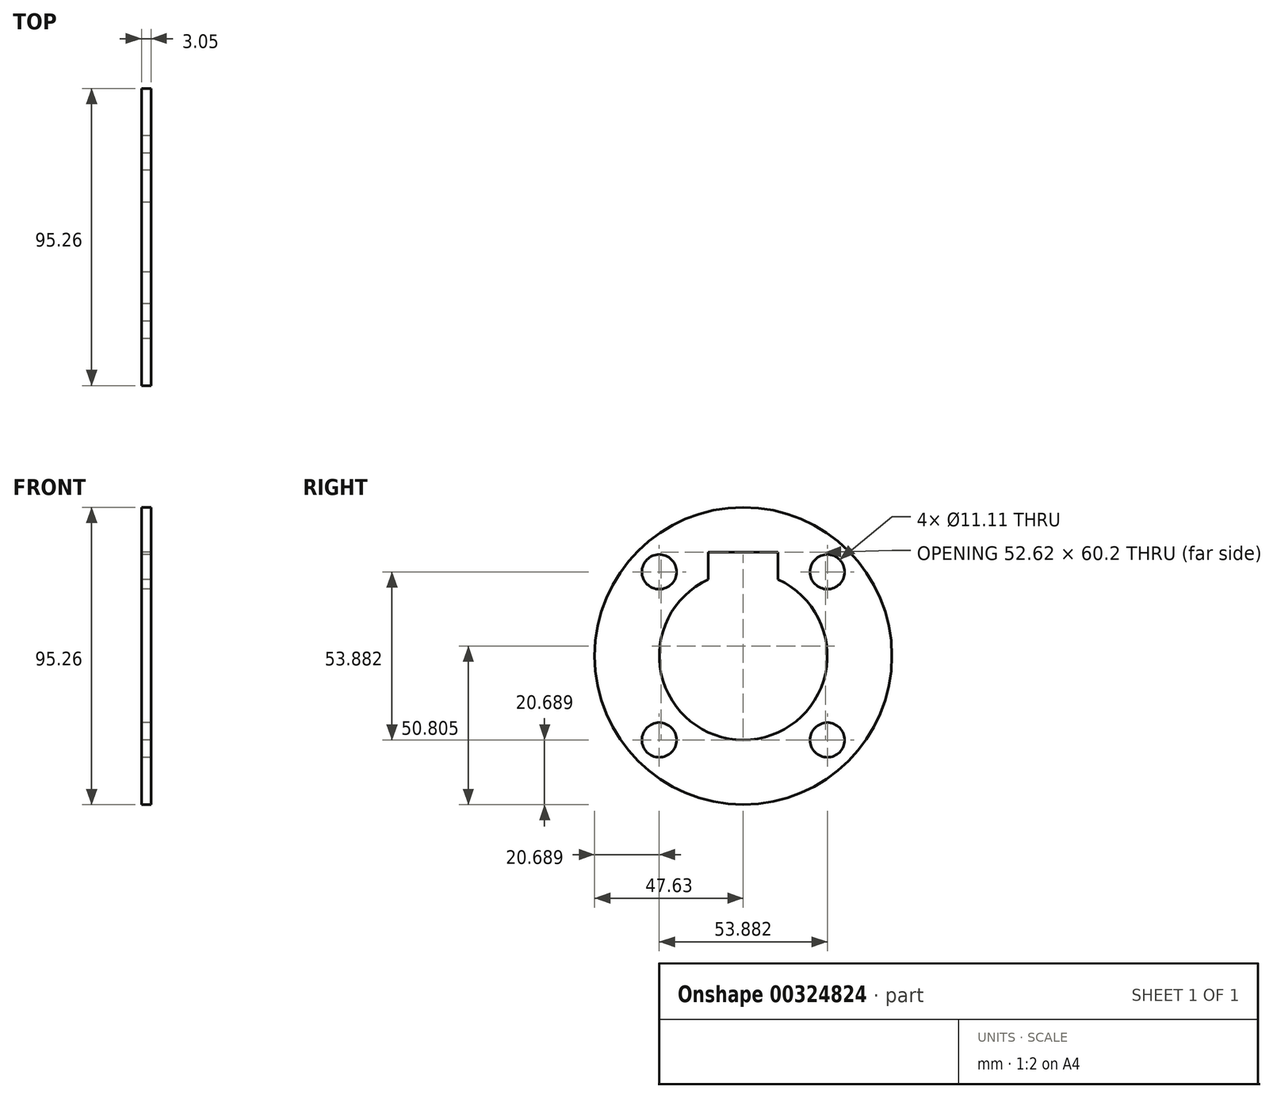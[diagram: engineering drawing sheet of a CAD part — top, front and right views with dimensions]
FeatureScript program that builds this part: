
annotation { "Feature Type Name" : "Feature", "Feature Type Description" : "" }
export const myFeature = defineFeature(function(context is Context, id is Id, definition is map)
    precondition{}
    {
        {
            var Q0;
            Q0=qCreatedBy(makeId("Right.planeOp"),FACE);
            var sketch = newSketch(context, id + "F0", { "sketchPlane" : qUnion([Q0])});
            skCircle(sketch, "E0", {"center": v(0, 0) * mm, "radius": 47.63 * mm});
            skArc(sketch, "E1", {"start": v(-11.18, 24.5) * mm, "mid": v(0, -26.92) * mm, "end": v(11.18, 24.5) * mm});
            skLineSegment(sketch, "E2", {"start": v(0, 0) * mm, "end": v(70.22, 0) * mm, "construction": true});
            skLineSegment(sketch, "E3", {"start": v(0, 0) * mm, "end": v(0, 59.17) * mm, "construction": true});
            skLineSegment(sketch, "E4.0", {"start": v(0, 33.27) * mm, "end": v(70.22, 33.27) * mm, "construction": true});
            skLineSegment(sketch, "E5.0", {"start": v(11.18, 0) * mm, "end": v(11.18, 20.57) * mm, "construction": true});
            skLineSegment(sketch, "E6.bottom", {"start": v(11.18, 33.27) * mm, "end": v(-11.18, 33.27) * mm});
            skLineSegment(sketch, "E6.left", {"start": v(11.18, 33.27) * mm, "end": v(11.18, 20.57) * mm});
            skLineSegment(sketch, "E6.right", {"start": v(-11.18, 33.27) * mm, "end": v(-11.18, 24.5) * mm});
            skLineSegment(sketch, "E7.trimOffspring", {"start": v(11.18, 24.5) * mm, "end": v(11.18, 59.17) * mm, "construction": true});
            skCircle(sketch, "E8", {"center": v(0, 0) * mm, "radius": 38.1 * mm, "construction": true});
            skLineSegment(sketch, "E9", {"start": v(0, 0) * mm, "end": v(-42.76, 42.76) * mm, "construction": true});
            skLineSegment(sketch, "E10", {"start": v(-42.76, 42.76) * mm, "end": v(-17.32, 57.62) * mm, "construction": true});
            skPoint(sketch, "E11", {"position": v(-26.94, 26.94) * mm});
            skPoint(sketch, "E12.1.0", {"position": v(-26.94, -26.94) * mm});
            skPoint(sketch, "E12.2.0", {"position": v(26.94, -26.94) * mm});
            skPoint(sketch, "E12.3.0", {"position": v(26.94, 26.94) * mm});
            skCircle(sketch, "E13", {"center": v(-26.94, 26.94) * mm, "radius": 5.56 * mm});
            skCircle(sketch, "E14", {"center": v(-26.94, -26.94) * mm, "radius": 5.56 * mm});
            skCircle(sketch, "E15", {"center": v(26.94, -26.94) * mm, "radius": 5.56 * mm});
            skCircle(sketch, "E16", {"center": v(26.94, 26.94) * mm, "radius": 5.56 * mm});
            skSolve(sketch);
        }
        {
            var Q0;
            Q0=qSketchRegion(id+"F0",true);
            extrude(context, id + "F1", {"entities" : qUnion([Q0]), "depth" : 3.05 * mm});
        }
    });
